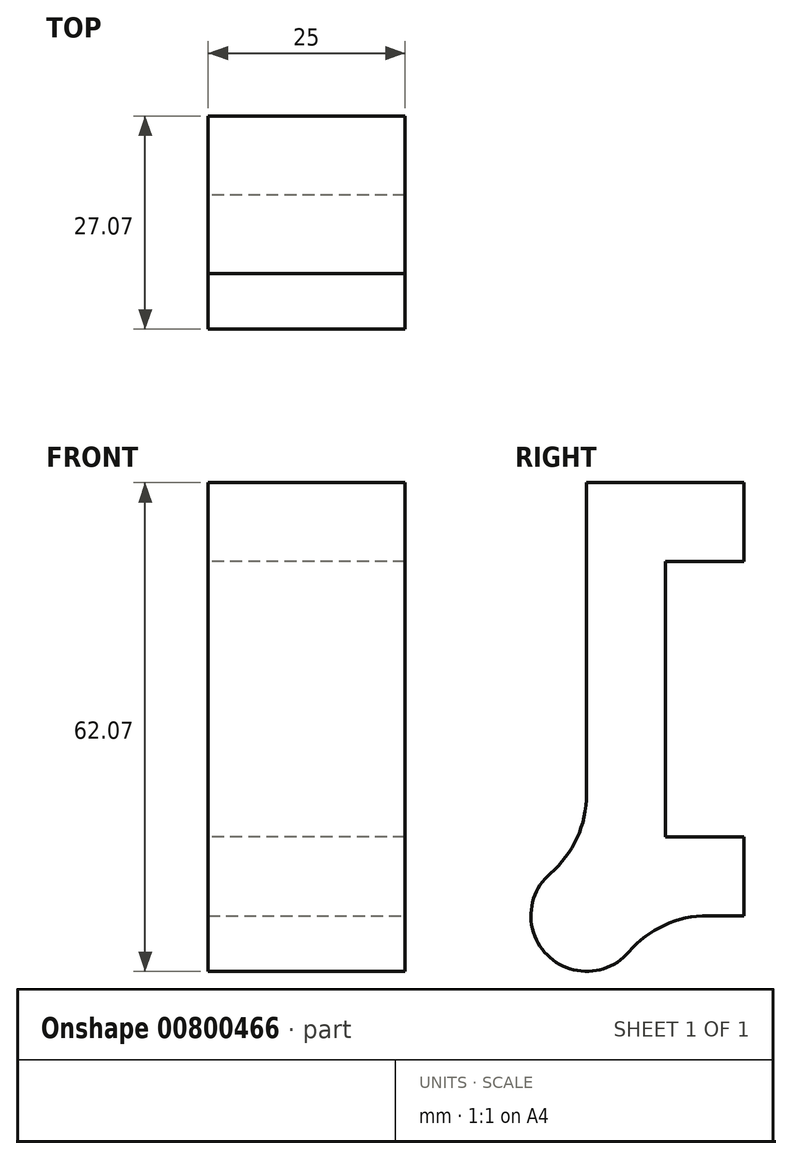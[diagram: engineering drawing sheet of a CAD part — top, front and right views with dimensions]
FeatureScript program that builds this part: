
annotation { "Feature Type Name" : "Feature", "Feature Type Description" : "" }
export const myFeature = defineFeature(function(context is Context, id is Id, definition is map)
    precondition{}
    {
        {
            var Q0;
            Q0=qCreatedBy(makeId("Right.planeOp"),FACE);
            var sketch = newSketch(context, id + "F0", { "sketchPlane" : qUnion([Q0])});
            skLineSegment(sketch, "E0", {"start": v(0, 0) * mm, "end": v(0, 35) * mm});
            skLineSegment(sketch, "E1", {"start": v(0, 35) * mm, "end": v(10, 35) * mm});
            skLineSegment(sketch, "E2", {"start": v(10, 35) * mm, "end": v(10, 45) * mm});
            skLineSegment(sketch, "E3", {"start": v(10, 45) * mm, "end": v(-10, 45) * mm});
            skLineSegment(sketch, "E4", {"start": v(-10, 45) * mm, "end": v(-10, -10) * mm});
            skLineSegment(sketch, "E5", {"start": v(-10, -10) * mm, "end": v(10, -10) * mm});
            skLineSegment(sketch, "E6", {"start": v(10, -10) * mm, "end": v(10, 0) * mm});
            skLineSegment(sketch, "E7", {"start": v(10, 0) * mm, "end": v(0, 0) * mm});
            skLineSegment(sketch, "E8", {"start": v(0, 0) * mm, "end": v(-10, -10) * mm, "construction": true});
            skPoint(sketch, "E9", {"position": v(-5, -5) * mm});
            skCircle(sketch, "E10", {"center": v(-10, -10) * mm, "radius": 7.07 * mm});
            skSolve(sketch);
        }
        {
            var Q0;
            Q0=makeQuery(id+"F0.imprint","IMPRINT",FACE,{"disambiguationData":[TD([[makeQuery(id+"F0.imprint","IMPRINT",EDGE,{"derivedFrom":sQuery(id+"F0.wireOp",EDGE,"E0")}),1.0]])]});
            var Q1;
            {var subQ0=sQuery(id+"F0.wireOp",EDGE,"E5");var subQ1=sQuery(id+"F0.wireOp",EDGE,"E4");var subQ2=makeQuery(id+"F0.imprint","INTERSECT",VERTEX,{"derivedFrom":[subQ1,subQ0]});Q1=makeQuery(id+"F0.imprint","IMPRINT",FACE,{"disambiguationData":[TD([[makeQuery(id+"F0.imprint","IMPRINT",EDGE,{"disambiguationData":[TD([[subQ2,1.0]])],"derivedFrom":subQ1}),1.0]])]});}
            var Q2;
            {var subQ0=sQuery(id+"F0.wireOp",EDGE,"E5");var subQ1=sQuery(id+"F0.wireOp",EDGE,"E4");var subQ2=makeQuery(id+"F0.imprint","INTERSECT",VERTEX,{"derivedFrom":[subQ1,subQ0]});Q2=makeQuery(id+"F0.imprint","IMPRINT",FACE,{"disambiguationData":[TD([[makeQuery(id+"F0.imprint","IMPRINT",EDGE,{"disambiguationData":[TD([[subQ2,1.0]])],"derivedFrom":subQ1}),-1.0]])]});}
            extrude(context, id + "F1", {"entities" : qUnion([Q0, Q1, Q2]), "depth" : 25 * mm, "offsetDistance" : 25 * mm});
        }
        {
            var Q0;
            Q0=makeQuery(id+"F1.opExtrude","SWEPT_EDGE",EDGE,{"disambiguationData":[OSD([sQuery(id+"F0.wireOp",EDGE,"E4"),sQuery(id+"F0.wireOp",EDGE,"E10")])]});
            var Q1;
            Q1=makeQuery(id+"F1.opExtrude","SWEPT_EDGE",EDGE,{"disambiguationData":[OSD([sQuery(id+"F0.wireOp",EDGE,"E5"),sQuery(id+"F0.wireOp",EDGE,"E10")])]});
            fillet(context, id + "F2", {"entities" : qUnion([Q0, Q1]), "radius" : 13.28 * mm, "tangentPropagation" : true, "allowEdgeOverflow" : false});
        }
    });
